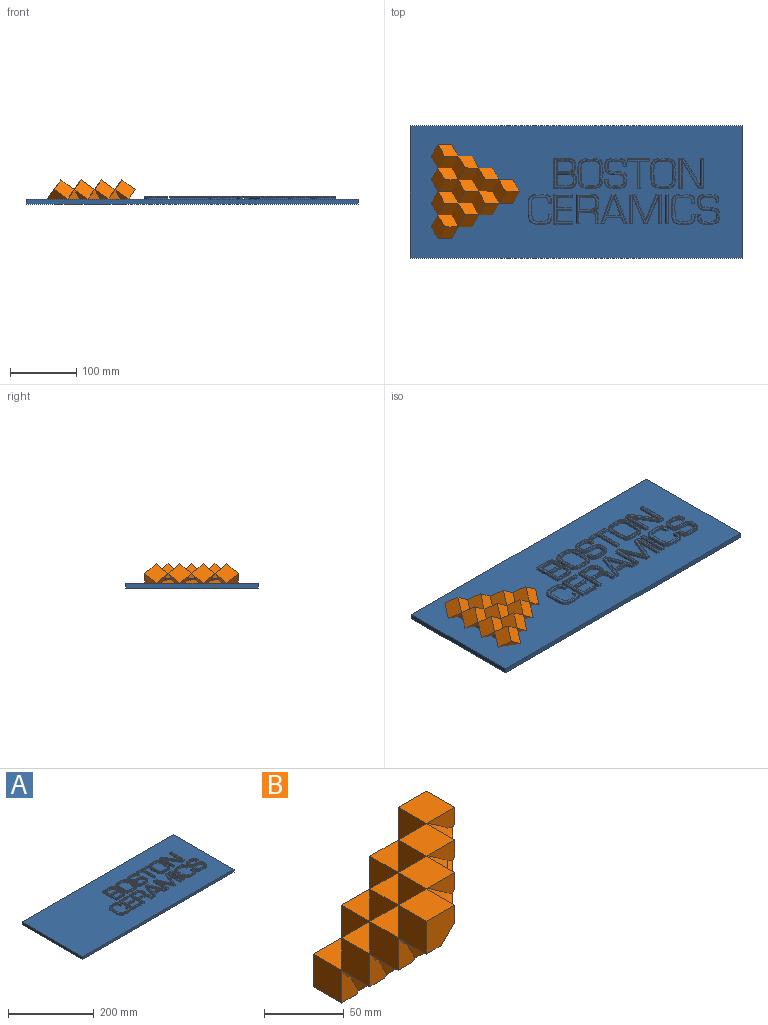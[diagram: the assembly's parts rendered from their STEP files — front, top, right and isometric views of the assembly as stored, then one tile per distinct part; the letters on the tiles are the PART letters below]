
ASSEMBLY  parts=2 mates=1
PART A: 238 faces, bbox 500x200x11.5 mm
  f0: cylinder r=1mm len=4.67mm, axis (-1,0,0), area 6.5mm2, adj f100,f101,f104,f198
  f1: cylinder r=1mm len=4.89mm, axis (1,0,0), area 6.9mm2, adj f100,f101,f102,f198
  f2: cylinder r=1mm len=4.67mm, axis (-1,0,0), area 6.5mm2, adj f119,f120,f123,f142
  f3: cylinder r=1mm len=4.89mm, axis (1,0,0), area 6.9mm2, adj f119,f120,f121,f142
  f4: plane 42.42x3.11mm, normal (0,0,1), area 132mm2, adj f147,f148,f150,f151
  f5: plane 42.42x39.02mm, normal (0,0,1), area 260mm2, adj f149,f151,f152,f155,f156,f158,f159
  f6: extruded ~16.02x7.64mm, area 77.2mm2, adj f7,f18,f20,f225
  f7: plane 16.61x3mm, normal (0,1,0), area 49.8mm2, adj f6,f8,f20,f226
  f8: plane 15.99x3mm, normal (1,0,0), area 48mm2, adj f7,f18,f20,f228
  f9: plane 20.32x3mm, normal (0,1,0), area 61mm2, adj f10,f16,f22,f232
  f10: plane 44.58x3mm, normal (-1,0,0), area 133.7mm2, adj f9,f11,f22,f230
  f11: plane 21.87x3mm, normal (0,-1,0), area 65.6mm2, adj f10,f12,f22,f229
  f12: extruded ~23.45x12.2mm, area 103.5mm2, adj f11,f16,f22,f231
  f13: plane 15.58x3mm, normal (0,-1,0), area 46.7mm2, adj f14,f17,f21,f235
  f14: extruded ~15.22x7.31mm, area 69.4mm2, adj f13,f15,f21,f234
  f15: plane 17.44x3mm, normal (0,1,0), area 52.3mm2, adj f14,f17,f21,f236
  f16: extruded ~21.25x12.24mm, area 96.5mm2, adj f9,f12,f22,f233
  f17: plane 15.17x3mm, normal (1,0,0), area 45.5mm2, adj f13,f15,f21,f237
  f18: plane 17.44x3mm, normal (0,-1,0), area 52.3mm2, adj f6,f8,f20,f227
  f19: plane 42.71x32.08mm, normal (0,0,1), area 407.7mm2, adj f225,f226,f227,f228,f229,f230,f231,f232
  f20: plane 24.31x16.07mm, normal (0,0,1), area 374.4mm2, adj f6,f7,f8,f18
  f21: plane 22.9x15.26mm, normal (0,0,1), area 333.6mm2, adj f13,f14,f15,f17
  f22: plane 500x200mm, normal (0,0,1), area 88572.9mm2, adj f9,f10,f11,f12,f16,f23,f24,f25
  f23: plane 33.72x3mm, normal (0,1,0), area 101.2mm2, adj f22,f24,f30,f214
  f24: plane 4.99x3mm, normal (-1,0.01,0), area 15mm2, adj f22,f23,f25,f212
  f25: plane 14.67x3mm, normal (0,-1,0), area 44mm2, adj f22,f24,f26,f211
  f26: plane 39.76x3mm, normal (-1,0,0), area 119.3mm2, adj f22,f25,f27,f213
  f27: plane 5x3mm, normal (0,-1,0), area 15mm2, adj f22,f26,f28,f215
  f28: plane 39.69x3mm, normal (1,0,0), area 119.1mm2, adj f22,f27,f29,f217
  f29: plane 14.1x3mm, normal (0,-1,0), area 42.3mm2, adj f22,f28,f30,f218
  f30: plane 5.06x3mm, normal (1,0,0), area 15.2mm2, adj f22,f23,f29,f216
  f31: plane 42.75x31.77mm, normal (0,0,1), area 215.4mm2, adj f211,f212,f213,f214,f215,f216,f217,f218
  f32: plane 4.89x3mm, normal (-0.01,-1,0), area 14.7mm2, adj f22,f33,f41,f204
  f33: plane 39.65x3mm, normal (1,0,0), area 118.9mm2, adj f22,f32,f34,f202
  f34: plane 39.63x24.41mm, normal (-0.85,-0.52,0), area 139.6mm2, adj f22,f33,f35,f200
  f35: plane 8.43x3mm, normal (-0.01,-1,0), area 25.3mm2, adj f22,f34,f36,f199
  f36: plane 44.65x3mm, normal (1,0,0), area 133.9mm2, adj f22,f35,f37,f201
  f37: plane 5.36x3mm, normal (0.01,1,0), area 16.1mm2, adj f22,f36,f38,f203
  f38: plane 40.02x3mm, normal (-1,0,0), area 120.1mm2, adj f22,f37,f39,f205
  f39: plane 39.93x24.4mm, normal (0.85,0.52,0), area 140.4mm2, adj f22,f38,f40,f207
  f40: plane 8.16x3mm, normal (0.01,1,0), area 24.5mm2, adj f22,f39,f41,f208
  f41: plane 44.58x3mm, normal (-1,0,0), area 133.7mm2, adj f22,f32,f40,f206
  f42: plane 42.68x35.92mm, normal (0,0,1), area 425.7mm2, adj f199,f200,f201,f202,f203,f204,f205,f206
  f43: plane 5.28x3mm, normal (0,1,0), area 15.8mm2, adj f22,f44,f46,f143
  f44: plane 44.42x3mm, normal (-1,0,0), area 133.3mm2, adj f22,f43,f45,f144
  f45: plane 5.28x3mm, normal (0,-1,0), area 15.8mm2, adj f22,f44,f46,f146
  f46: plane 44.42x3mm, normal (1,0,0), area 133.3mm2, adj f22,f43,f45,f145
  f47: plane 42.42x3.28mm, normal (0,0,1), area 139.1mm2, adj f143,f144,f145,f146
  f48: plane 5.06x3mm, normal (0,-1,0), area 15.2mm2, adj f22,f49,f60,f154
  f49: plane 44.42x3mm, normal (1,0,0), area 133.3mm2, adj f22,f48,f50,f153
  f50: plane 8.71x3mm, normal (0,1,0), area 26.1mm2, adj f22,f49,f51,f156
  f51: plane 37.97x15.71mm, normal (-0.92,0.38,0), area 123.3mm2, adj f22,f50,f52,f152
  f52: plane 37.97x15.54mm, normal (0.93,0.38,0), area 123.1mm2, adj f22,f51,f53,f149
  f53: plane 8.55x3mm, normal (0,1,0), area 25.6mm2, adj f22,f52,f54,f151
  f54: plane 44.42x3mm, normal (-1,0,0), area 133.3mm2, adj f22,f53,f55,f148
  f55: plane 5.11x3mm, normal (0,-1,0), area 15.3mm2, adj f22,f54,f56,f147
  f56: plane 39.95x3mm, normal (1,0,0), area 119.9mm2, adj f22,f55,f57,f150
  f57: plane 39.95x16.67mm, normal (-0.92,-0.39,0), area 129.9mm2, adj f22,f56,f58,f155
  f58: plane 4.99x3mm, normal (0,-1,0), area 15mm2, adj f22,f57,f59,f158
  f59: plane 39.95x16.64mm, normal (0.92,-0.38,0), area 129.8mm2, adj f22,f58,f60,f159
  f60: plane 39.95x3mm, normal (-1,0,0), area 119.9mm2, adj f22,f48,f59,f157
  f61: plane 42.42x3.1mm, normal (0,0,1), area 130.7mm2, adj f153,f154,f156,f157
  f62: plane 26.37x9.54mm, normal (0.94,-0.34,0), area 84.1mm2, adj f63,f72,f74,f160
  f63: plane 26.39x9.72mm, normal (-0.94,-0.35,0), area 84.4mm2, adj f62,f72,f74,f162
  f64: plane 6.73x3mm, normal (0,1,0), area 20.2mm2, adj f22,f65,f71,f168
  f65: plane 44.42x16.23mm, normal (-0.94,0.34,0), area 141.9mm2, adj f22,f64,f66,f166
  f66: plane 5.52x3mm, normal (0,-1,0), area 16.5mm2, adj f22,f65,f67,f164
  f67: plane 9.01x3.29mm, normal (0.94,-0.34,0), area 28.8mm2, adj f22,f66,f68,f163
  f68: plane 22.27x3mm, normal (0,-1,0), area 66.8mm2, adj f22,f67,f69,f165
  f69: plane 8.99x3.35mm, normal (-0.94,-0.35,0), area 28.8mm2, adj f22,f68,f70,f167
  f70: plane 5.34x3mm, normal (0,-1,0), area 16mm2, adj f22,f69,f71,f169
  f71: plane 44.42x16.81mm, normal (0.94,0.35,0), area 142.5mm2, adj f22,f64,f70,f170
  f72: plane 19.26x3mm, normal (0,1,0), area 57.8mm2, adj f62,f63,f74,f161
  f73: plane 42.42x36.89mm, normal (0,0,1), area 317.8mm2, adj f160,f161,f162,f163,f164,f165,f166,f167
  f74: plane 26.39x19.26mm, normal (0,0,1), area 254mm2, adj f62,f63,f72
  f75: extruded ~11.86x6.85mm, area 46.5mm2, adj f22,f76,f89,f178
  f76: extruded ~24.51x10.9mm, area 105.1mm2, adj f22,f75,f77,f176
  f77: plane 23.03x3mm, normal (0,1,0), area 69.1mm2, adj f22,f76,f78,f174
  f78: plane 44.44x3mm, normal (-1,0,0), area 133.3mm2, adj f22,f77,f79,f172
  f79: plane 4.81x3mm, normal (0,-1,0), area 14.4mm2, adj f22,f78,f80,f171
  f80: plane 17.8x3mm, normal (1,0,0), area 53.4mm2, adj f22,f79,f81,f173
  f81: plane 17.01x3mm, normal (0,-1,0), area 51mm2, adj f22,f80,f82,f175
  f82: extruded ~7.19x6.49mm, area 33mm2, adj f22,f81,f83,f177
  f83: plane 10.65x3mm, normal (-1,0,0), area 32mm2, adj f22,f82,f84,f179
  f84: plane 4.98x3mm, normal (0,-1,0), area 15mm2, adj f22,f83,f89,f181
  f85: plane 17.9x3mm, normal (0,-1,0), area 53.7mm2, adj f86,f88,f137,f183
  f86: extruded ~17.86x7.26mm, area 77.4mm2, adj f85,f87,f137,f182
  f87: plane 16.93x3mm, normal (0,1,0), area 50.8mm2, adj f86,f88,f137,f184
  f88: plane 17.74x3mm, normal (1,0,0), area 53.2mm2, adj f85,f87,f137,f185
  f89: plane 8.06x3mm, normal (1,0,0), area 24.2mm2, adj f22,f75,f84,f180
  f90: plane 42.44x31.93mm, normal (0,0,1), area 353.3mm2, adj f171,f172,f173,f174,f175,f176,f177,f178
  f91: plane 36.67x28.33mm, normal (0,0,1), area 965.5mm2, adj f113
  f92: extruded ~36.57x28.14mm, area 346.1mm2, adj f110,f209
  f93: extruded ~45.26x37.8mm, area 443.4mm2, adj f22,f210
  f94: plane 43.28x35.81mm, normal (0,0,1), area 330mm2, adj f209,f210
  f95: plane 500x200mm, normal (0,0,-1), area 100000mm2, adj f96,f97,f98,f99
  f96: plane 500x7.5mm, normal (0,-1,0), area 3750mm2, adj f22,f95,f97,f99
  f97: plane 200x7.5mm, normal (-1,0,0), area 1500mm2, adj f22,f95,f96,f98
  f98: plane 500x7.5mm, normal (0,1,0), area 3750mm2, adj f22,f95,f97,f99
  f99: plane 200x7.5mm, normal (1,0,0), area 1500mm2, adj f22,f95,f96,f98
  f100: plane 43.27x33.69mm, normal (0,0,1), area 409mm2, adj f0,f1,f101,f198
  f101: extruded ~36.26x25.62mm, area 382.1mm2, adj f0,f1,f22,f100,f102,f104
  f102: plane 4.89x3mm, normal (0,1,0), area 14.7mm2, adj f1,f22,f101,f103
  f103: extruded ~45.23x35.68mm, area 374.4mm2, adj f22,f102,f104,f198
  f104: plane 4.6x3mm, normal (0,-1,0), area 13.8mm2, adj f0,f22,f101,f103
  f105: plane 43.39x31.43mm, normal (0,0,1), area 343.4mm2, adj f138,f139,f140,f141
  f106: extruded ~40.76x33.41mm, area 380.7mm2, adj f22,f107,f109,f139
  f107: plane 5.01x3mm, normal (0,1,0), area 15mm2, adj f22,f106,f108,f141
  f108: extruded ~41.05x32.28mm, area 367.9mm2, adj f22,f107,f109,f140
  f109: plane 4.68x3mm, normal (0,-1,0), area 14mm2, adj f22,f106,f108,f138
  f110: plane 36.67x28.33mm, normal (0,0,1), area 965.5mm2, adj f92
  f111: plane 43.28x35.81mm, normal (0,0,1), area 330mm2, adj f223,f224
  f112: extruded ~45.26x37.8mm, area 443.4mm2, adj f22,f224
  f113: extruded ~36.57x28.14mm, area 346.1mm2, adj f91,f223
  f114: plane 43.39x31.43mm, normal (0,0,1), area 343.4mm2, adj f219,f220,f221,f222
  f115: extruded ~40.76x33.41mm, area 380.7mm2, adj f22,f116,f118,f220
  f116: plane 5.01x3mm, normal (0,1,0), area 15mm2, adj f22,f115,f117,f222
  f117: extruded ~41.05x32.28mm, area 367.9mm2, adj f22,f116,f118,f221
  f118: plane 4.68x3mm, normal (0,-1,0), area 14mm2, adj f22,f115,f117,f219
  f119: plane 43.27x33.69mm, normal (0,0,1), area 409mm2, adj f2,f3,f120,f142
  f120: extruded ~36.26x25.62mm, area 382.1mm2, adj f2,f3,f22,f119,f121,f123
  f121: plane 4.89x3mm, normal (0,1,0), area 14.7mm2, adj f3,f22,f120,f122
  f122: extruded ~45.23x35.68mm, area 374.4mm2, adj f22,f121,f123,f142
  f123: plane 4.6x3mm, normal (0,-1,0), area 13.8mm2, adj f2,f22,f120,f122
  f124: plane 42.54x26.48mm, normal (0,0,1), area 293.4mm2, adj f186,f187,f188,f189,f190,f191,f192,f193
  f125: plane 23.44x3mm, normal (0,-1,0), area 70.3mm2, adj f22,f126,f136,f195
  f126: plane 14.97x3mm, normal (1,0,0), area 44.9mm2, adj f22,f125,f127,f197
  f127: plane 22.3x3mm, normal (0,1,0), area 66.9mm2, adj f22,f126,f128,f196
  f128: plane 4.48x3mm, normal (1,0,0), area 13.4mm2, adj f22,f127,f129,f194
  f129: plane 22.3x3mm, normal (0,-1,0), area 66.9mm2, adj f22,f128,f130,f192
  f130: plane 16.44x3mm, normal (1,0,0), area 49.3mm2, adj f22,f129,f131,f190
  f131: plane 23.28x3mm, normal (0,1,0), area 69.8mm2, adj f22,f130,f132,f188
  f132: plane 4.31x3mm, normal (1,0,0), area 12.9mm2, adj f22,f131,f133,f186
  f133: plane 28.32x3mm, normal (0,-1,0), area 85mm2, adj f22,f132,f134,f187
  f134: plane 44.54x3mm, normal (-1,0,0), area 133.6mm2, adj f22,f133,f135,f189
  f135: plane 28.48x3mm, normal (0,1,0), area 85.4mm2, adj f22,f134,f136,f191
  f136: plane 4.34x3mm, normal (1,0,0), area 13mm2, adj f22,f125,f135,f193
  f137: plane 24.24x17.91mm, normal (0,0,1), area 410.3mm2, adj f85,f86,f87,f88
  f138: cylinder r=1mm len=4.68mm, axis (-1,0,0), area 5.9mm2, adj f105,f109,f139,f140
  f139: bspline ~41.76x33.43mm, area 197.6mm2, adj f105,f106,f138,f141
  f140: bspline ~42.11x32.36mm, area 197.9mm2, adj f105,f108,f138,f141
  f141: cylinder r=1mm len=5.01mm, axis (1,0,0), area 6.4mm2, adj f105,f107,f139,f140
  f142: bspline ~45.27x35.69mm, area 193.2mm2, adj f2,f3,f119,f122
  f143: cylinder r=1mm len=5.28mm, axis (1,0,0), area 6.7mm2, adj f43,f47,f144,f145
  f144: cylinder r=1mm len=44.42mm, axis (0,1,0), area 68.2mm2, adj f44,f47,f143,f146
  f145: cylinder r=1mm len=44.42mm, axis (0,-1,0), area 68.2mm2, adj f46,f47,f143,f146
  f146: cylinder r=1mm len=5.28mm, axis (-1,0,0), area 6.7mm2, adj f45,f47,f144,f145
  f147: cylinder r=1mm len=5.11mm, axis (-1,0,0), area 6.5mm2, adj f4,f55,f148,f150
  f148: cylinder r=1mm len=44.42mm, axis (0,1,0), area 68.2mm2, adj f4,f54,f147,f151
  f149: cylinder r=1mm len=40.6mm, axis (0.38,-0.93,0), area 65.8mm2, adj f5,f52,f151,f152
  f150: cylinder r=1mm len=43.68mm, axis (0,-1,0), area 64.8mm2, adj f4,f56,f147,f151,f155
  f151: cylinder r=1mm len=8.55mm, axis (1,0,0), area 12.2mm2, adj f4,f5,f53,f148,f149,f150,f155
  f152: cylinder r=1mm len=40.6mm, axis (0.38,0.92,0), area 65.9mm2, adj f5,f51,f149,f156
  f153: cylinder r=1mm len=44.42mm, axis (0,-1,0), area 68.2mm2, adj f49,f61,f154,f156
  f154: cylinder r=1mm len=5.06mm, axis (-1,0,0), area 6.4mm2, adj f48,f61,f153,f157
  f155: cylinder r=1mm len=43.78mm, axis (-0.39,0.92,0), area 70.1mm2, adj f5,f57,f150,f151,f158
  f156: cylinder r=1mm len=8.71mm, axis (1,0,0), area 12.5mm2, adj f5,f50,f61,f152,f153,f157,f159
  f157: cylinder r=1mm len=43.68mm, axis (0,1,0), area 64.8mm2, adj f60,f61,f154,f156,f159
  f158: cylinder r=1mm len=4.99mm, axis (-1,0,0), area 6.8mm2, adj f5,f58,f155,f159
  f159: cylinder r=1mm len=43.78mm, axis (-0.38,-0.92,0), area 70.1mm2, adj f5,f59,f156,f157,f158
  f160: cylinder r=1mm len=30.63mm, axis (-0.34,-0.94,0), area 47.3mm2, adj f62,f73,f161,f162
  f161: cylinder r=1mm len=22.12mm, axis (1,0,0), area 32.5mm2, adj f72,f73,f160,f162
  f162: cylinder r=1mm len=30.65mm, axis (-0.35,0.94,0), area 47.4mm2, adj f63,f73,f160,f161
  f163: cylinder r=1mm len=10.01mm, axis (-0.34,-0.94,0), area 15.1mm2, adj f67,f73,f164,f165
  f164: cylinder r=1mm len=5.52mm, axis (-1,0,0), area 7mm2, adj f66,f73,f163,f166
  f165: cylinder r=1mm len=23.67mm, axis (-1,0,0), area 36.1mm2, adj f68,f73,f163,f167
  f166: cylinder r=1mm len=44.76mm, axis (0.34,0.94,0), area 72.6mm2, adj f65,f73,f164,f168
  f167: cylinder r=1mm len=9.99mm, axis (-0.35,0.94,0), area 15.1mm2, adj f69,f73,f165,f169
  f168: cylinder r=1mm len=6.73mm, axis (1,0,0), area 9.5mm2, adj f64,f73,f166,f170
  f169: cylinder r=1mm len=5.34mm, axis (-1,0,0), area 6.7mm2, adj f70,f73,f167,f170
  f170: cylinder r=1mm len=44.77mm, axis (0.35,-0.94,0), area 72.9mm2, adj f71,f73,f168,f169
  f171: cylinder r=1mm len=4.81mm, axis (-1,0,0), area 6mm2, adj f79,f90,f172,f173
  f172: cylinder r=1mm len=44.44mm, axis (0,1,0), area 68.2mm2, adj f78,f90,f171,f174
  f173: cylinder r=1mm len=18.81mm, axis (0,-1,0), area 28mm2, adj f80,f90,f171,f175
  f174: cylinder r=1mm len=23.03mm, axis (1,0,0), area 35.4mm2, adj f77,f90,f172,f176
  f175: cylinder r=1mm len=18.01mm, axis (-1,0,0), area 27.5mm2, adj f81,f90,f173,f177
  f176: bspline ~25.88x13.96mm, area 57.5mm2, adj f76,f90,f174,f178
  f177: bspline ~8.67x7.78mm, area 18.2mm2, adj f82,f90,f175,f179
  f178: bspline ~24.13x15.38mm, area 27.7mm2, adj f75,f90,f176,f180
  f179: cylinder r=1mm len=10.65mm, axis (0,1,0), area 15.9mm2, adj f83,f90,f177,f181
  f180: cylinder r=1mm len=8.09mm, axis (0,-1,0), area 11.9mm2, adj f89,f90,f178,f181
  f181: cylinder r=1mm len=4.98mm, axis (-1,0,0), area 6.3mm2, adj f84,f90,f179,f180
  f182: bspline ~19.95x10.14mm, area 42.4mm2, adj f86,f90,f183,f184
  f183: cylinder r=1mm len=18.9mm, axis (-1,0,0), area 28.8mm2, adj f85,f90,f182,f185
  f184: cylinder r=1mm len=17.95mm, axis (1,0,0), area 27.4mm2, adj f87,f90,f182,f185
  f185: cylinder r=1mm len=19.74mm, axis (0,-1,0), area 29.4mm2, adj f88,f90,f183,f184
  f186: cylinder r=1mm len=4.31mm, axis (0,-1,0), area 5.2mm2, adj f124,f132,f187,f188
  f187: cylinder r=1mm len=28.32mm, axis (-1,0,0), area 42.9mm2, adj f124,f133,f186,f189
  f188: cylinder r=1mm len=24.28mm, axis (1,0,0), area 36.6mm2, adj f124,f131,f186,f190
  f189: cylinder r=1mm len=44.54mm, axis (0,1,0), area 68.4mm2, adj f124,f134,f187,f191
  f190: cylinder r=1mm len=18.44mm, axis (0,-1,0), area 27.4mm2, adj f124,f130,f188,f192
  f191: cylinder r=1mm len=28.48mm, axis (1,0,0), area 43.2mm2, adj f124,f135,f189,f193
  f192: cylinder r=1mm len=23.3mm, axis (-1,0,0), area 35mm2, adj f124,f129,f190,f194
  f193: cylinder r=1mm len=4.34mm, axis (0,-1,0), area 5.2mm2, adj f124,f136,f191,f195
  f194: cylinder r=1mm len=4.48mm, axis (0,-1,0), area 5.5mm2, adj f124,f128,f192,f196
  f195: cylinder r=1mm len=24.44mm, axis (-1,0,0), area 36.8mm2, adj f124,f125,f193,f197
  f196: cylinder r=1mm len=23.3mm, axis (1,0,0), area 35mm2, adj f124,f127,f194,f197
  f197: cylinder r=1mm len=16.97mm, axis (0,-1,0), area 25.1mm2, adj f124,f126,f195,f196
  f198: bspline ~45.27x35.69mm, area 193.2mm2, adj f0,f1,f100,f103
  f199: cylinder r=1mm len=8.44mm, axis (-1,0.01,0), area 12mm2, adj f35,f42,f200,f201
  f200: cylinder r=1mm len=43.13mm, axis (-0.52,0.85,0), area 75.4mm2, adj f34,f42,f199,f202
  f201: cylinder r=1mm len=44.65mm, axis (0,-1,0), area 68.6mm2, adj f36,f42,f199,f203
  f202: cylinder r=1mm len=43.15mm, axis (0,-1,0), area 64.2mm2, adj f33,f42,f200,f204
  f203: cylinder r=1mm len=5.37mm, axis (1,-0.01,0), area 6.8mm2, adj f37,f42,f201,f205
  f204: cylinder r=1mm len=4.9mm, axis (-1,0.01,0), area 6.1mm2, adj f32,f42,f202,f206
  f205: cylinder r=1mm len=43.58mm, axis (0,1,0), area 64.9mm2, adj f38,f42,f203,f207
  f206: cylinder r=1mm len=44.58mm, axis (0,1,0), area 68.5mm2, adj f41,f42,f204,f208
  f207: cylinder r=1mm len=43.49mm, axis (0.52,-0.85,0), area 75.9mm2, adj f39,f42,f205,f208
  f208: cylinder r=1mm len=8.17mm, axis (1,-0.01,0), area 11.6mm2, adj f40,f42,f206,f207
  f209: bspline ~38.58x30.17mm, area 186mm2, adj f92,f94
  f210: bspline ~45.28x37.81mm, area 223.6mm2, adj f93,f94
  f211: cylinder r=1mm len=15.67mm, axis (-1,0,0), area 23mm2, adj f25,f31,f212,f213
  f212: cylinder r=1mm len=5mm, axis (0.01,1,0), area 6.3mm2, adj f24,f31,f211,f214
  f213: cylinder r=1mm len=40.76mm, axis (0,1,0), area 62.5mm2, adj f26,f31,f211,f215
  f214: cylinder r=1mm len=33.72mm, axis (1,0,0), area 51.4mm2, adj f23,f31,f212,f216
  f215: cylinder r=1mm len=5mm, axis (-1,0,0), area 6.3mm2, adj f27,f31,f213,f217
  f216: cylinder r=1mm len=5.06mm, axis (0,-1,0), area 6.4mm2, adj f30,f31,f214,f218
  f217: cylinder r=1mm len=40.69mm, axis (0,-1,0), area 62.3mm2, adj f28,f31,f215,f218
  f218: cylinder r=1mm len=15.1mm, axis (-1,0,0), area 22.1mm2, adj f29,f31,f216,f217
  f219: cylinder r=1mm len=4.68mm, axis (-1,0,0), area 5.9mm2, adj f114,f118,f220,f221
  f220: bspline ~41.76x33.43mm, area 197.6mm2, adj f114,f115,f219,f222
  f221: bspline ~42.11x32.36mm, area 197.9mm2, adj f114,f117,f219,f222
  f222: cylinder r=1mm len=5.01mm, axis (1,0,0), area 6.4mm2, adj f114,f116,f220,f221
  f223: bspline ~38.58x30.17mm, area 186mm2, adj f111,f113
  f224: bspline ~45.28x37.81mm, area 223.6mm2, adj f111,f112
  f225: bspline ~18.04x9.28mm, area 42.2mm2, adj f6,f19,f226,f227
  f226: cylinder r=1mm len=17.63mm, axis (1,0,0), area 26.9mm2, adj f7,f19,f225,f228
  f227: cylinder r=1mm len=18.44mm, axis (-1,0,0), area 28.2mm2, adj f18,f19,f225,f228
  f228: cylinder r=1mm len=17.99mm, axis (0,-1,0), area 26.7mm2, adj f8,f19,f226,f227
  f229: cylinder r=1mm len=21.92mm, axis (-1,0,0), area 33.6mm2, adj f11,f19,f230,f231
  f230: cylinder r=1mm len=44.58mm, axis (0,1,0), area 68.5mm2, adj f10,f19,f229,f232
  f231: bspline ~26.17x15.33mm, area 54.5mm2, adj f12,f19,f229,f233
  f232: cylinder r=1mm len=20.32mm, axis (1,0,0), area 31.1mm2, adj f9,f19,f230,f233
  f233: bspline ~23.51x14.63mm, area 50.9mm2, adj f16,f19,f231,f232
  f234: bspline ~17.35x8.85mm, area 38.1mm2, adj f14,f19,f235,f236
  f235: cylinder r=1mm len=16.58mm, axis (-1,0,0), area 25.2mm2, adj f13,f19,f234,f237
  f236: cylinder r=1mm len=18.53mm, axis (1,0,0), area 28.3mm2, adj f15,f19,f234,f237
  f237: cylinder r=1mm len=17.17mm, axis (0,-1,0), area 25.4mm2, adj f17,f19,f235,f236
PART B: 79 faces, bbox 100x100x100 mm
  f0: plane 23.19x23.19mm, normal (0.41,0.82,-0.41), area 279.7mm2, adj f14,f25,f77,f78
  f1: plane 23.19x23.19mm, normal (0.41,0.82,-0.41), area 279.7mm2, adj f23,f27,f76,f78
  f2: plane 23.19x23.19mm, normal (-0.82,-0.41,-0.41), area 279.1mm2, adj f7,f20,f74,f78
  f3: plane 23.19x23.19mm, normal (-0.82,-0.41,-0.41), area 279.1mm2, adj f6,f22,f73,f78
  f4: plane 23.19x23.19mm, normal (0.41,-0.41,0.82), area 105.9mm2, adj f8,f9,f19,f78
  f5: plane 23.19x23.19mm, normal (0.41,-0.41,0.82), area 105.9mm2, adj f11,f12,f18,f78
  f6: plane 24.66x14.91mm, normal (0,-1,0), area 217.6mm2, adj f3,f20,f31,f33,f55,f73,f78
  f7: plane 24.66x14.91mm, normal (0,-1,0), area 217.6mm2, adj f2,f28,f30,f33,f54,f74,f78
  f8: plane 24.09x14.91mm, normal (1,0,0), area 199.2mm2, adj f4,f19,f32,f34,f78
  f9: plane 24.09x14.91mm, normal (0,-1,0), area 199.2mm2, adj f4,f11,f19,f34,f78
  f10: plane 24.66x14.91mm, normal (0,-1,0), area 217.6mm2, adj f22,f33,f53,f56,f64,f72,f78
  f11: plane 24.09x14.91mm, normal (1,0,0), area 199.2mm2, adj f5,f9,f18,f34,f78
  f12: plane 24.09x14.91mm, normal (0,-1,0), area 199.2mm2, adj f5,f13,f18,f34,f78
  f13: plane 24.09x14.91mm, normal (1,0,0), area 199.2mm2, adj f12,f17,f34,f65,f78
  f14: plane 24.64x14.91mm, normal (1,0,0), area 215.8mm2, adj f0,f23,f29,f57,f62,f77,f78
  f15: plane 24.09x14.91mm, normal (0,-1,0), area 199.2mm2, adj f16,f17,f34,f65,f78
  f16: plane 25x25mm, normal (1,0,0), area 554.3mm2, adj f15,f25,f29,f34,f78
  f17: plane 19.1x19.1mm, normal (0.5,-0.5,0.71), area 257.5mm2, adj f13,f15,f34,f65
  f18: plane 19.1x19.1mm, normal (0.5,-0.5,0.71), area 257.5mm2, adj f5,f11,f12,f34
  f19: plane 19.1x19.1mm, normal (0.5,-0.5,0.71), area 257.5mm2, adj f4,f8,f9,f34
  f20: plane 24.65x14.91mm, normal (0,0,-1), area 215.3mm2, adj f2,f6,f30,f33,f54,f74,f78
  f21: plane 24.65x14.91mm, normal (0,0,-1), area 216.8mm2, adj f27,f29,f58,f60,f63,f75,f78
  f22: plane 24.65x14.91mm, normal (0,0,-1), area 215.3mm2, adj f3,f10,f31,f33,f55,f73,f78
  f23: plane 24.65x14.91mm, normal (0,0,-1), area 216.8mm2, adj f1,f14,f29,f59,f61,f76,f78
  f24: plane 24.65x14.91mm, normal (0,0,-1), area 215.3mm2, adj f32,f33,f53,f56,f64,f72,f78
  f25: plane 24.65x14.91mm, normal (0,0,-1), area 216.8mm2, adj f0,f16,f29,f57,f62,f77,f78
  f26: plane 24.64x14.91mm, normal (1,0,0), area 215.8mm2, adj f28,f29,f58,f60,f63,f75,f78
  f27: plane 24.64x14.91mm, normal (1,0,0), area 215.8mm2, adj f1,f21,f29,f59,f61,f76,f78
  f28: plane 25x25mm, normal (0,0,-1), area 554.3mm2, adj f7,f26,f29,f33,f78
  f29: plane 100x100mm, normal (0,1,0), area 2500.2mm2, adj f14,f16,f21,f23,f25,f26,f27,f28
  f30: plane 7.58x7.26mm, normal (0,-0.69,-0.72), area 25.9mm2, adj f7,f20,f54,f74
  f31: plane 7.58x7.26mm, normal (0,-0.69,-0.72), area 25.9mm2, adj f6,f22,f55,f73
  f32: plane 25x25mm, normal (0,-1,0), area 554.3mm2, adj f8,f24,f33,f34,f78
  f33: plane 100x100mm, normal (-1,0,0), area 2500.2mm2, adj f6,f7,f10,f20,f22,f24,f28,f29
  f34: plane 100x100mm, normal (0,0,1), area 2501.2mm2, adj f8,f9,f11,f12,f13,f15,f16,f17
  f35: plane 25x25mm, normal (-1,0,0), area 625mm2, adj f34,f36,f46,f50,f68
  f36: plane 25x25mm, normal (0,1,0), area 625mm2, adj f34,f35,f46,f48,f68
  f37: plane 25x25mm, normal (0,1,0), area 625mm2, adj f41,f42,f44,f46,f70
  f38: plane 25x25mm, normal (0,1,0), area 625mm2, adj f33,f39,f40,f45,f71
  f39: plane 25x25mm, normal (-1,0,0), area 625mm2, adj f29,f38,f40,f42,f71
  f40: plane 25x25mm, normal (0,0,1), area 625mm2, adj f29,f33,f38,f39,f71
  f41: plane 25x25mm, normal (-1,0,0), area 625mm2, adj f29,f37,f42,f52,f70
  f42: plane 25x25mm, normal (0,0,1), area 625mm2, adj f29,f37,f39,f41,f70
  f43: plane 25x25mm, normal (0,1,0), area 625mm2, adj f33,f44,f45,f49,f69
  f44: plane 25x25mm, normal (-1,0,0), area 625mm2, adj f37,f43,f45,f46,f69
  f45: plane 25x25mm, normal (0,0,1), area 625mm2, adj f33,f38,f43,f44,f69
  f46: plane 25x25mm, normal (0,0,1), area 625mm2, adj f35,f36,f37,f44,f68
  f47: plane 25x25mm, normal (0,1,0), area 625mm2, adj f33,f34,f48,f49,f67
  f48: plane 25x25mm, normal (-1,0,0), area 625mm2, adj f34,f36,f47,f49,f67
  f49: plane 25x25mm, normal (0,0,1), area 625mm2, adj f33,f43,f47,f48,f67
  f50: plane 25x25mm, normal (0,1,0), area 625mm2, adj f34,f35,f51,f52,f66
  f51: plane 25x25mm, normal (-1,0,0), area 625mm2, adj f29,f34,f50,f52,f66
  f52: plane 25x25mm, normal (0,0,1), area 625mm2, adj f29,f41,f50,f51,f66
  f53: plane 7.58x7.26mm, normal (0,-0.69,-0.72), area 25.9mm2, adj f10,f24,f56,f72
  f54: plane 7.58x7.26mm, normal (-0.71,-0.49,-0.51), area 38.9mm2, adj f7,f20,f30,f33
  f55: plane 7.58x7.26mm, normal (-0.71,-0.49,-0.51), area 38.9mm2, adj f6,f22,f31,f33
  f56: plane 7.58x7.26mm, normal (-0.71,-0.49,-0.51), area 38.9mm2, adj f10,f24,f33,f53
  f57: plane 7.49x7.36mm, normal (0.71,0,-0.7), area 25.8mm2, adj f14,f25,f62,f77
  f58: plane 7.49x7.36mm, normal (0.71,0,-0.7), area 25.8mm2, adj f21,f26,f60,f75
  f59: plane 7.49x7.36mm, normal (0.71,0,-0.7), area 25.8mm2, adj f23,f27,f61,f76
  f60: plane 7.49x7.36mm, normal (0.5,0.71,-0.5), area 38.9mm2, adj f21,f26,f29,f58
  f61: plane 7.49x7.36mm, normal (0.5,0.71,-0.5), area 38.9mm2, adj f23,f27,f29,f59
  f62: plane 7.49x7.36mm, normal (0.5,0.71,-0.5), area 38.9mm2, adj f14,f25,f29,f57
  f63: plane 23.19x23.19mm, normal (0.41,0.82,-0.41), area 279.7mm2, adj f21,f26,f75,f78
  f64: plane 23.19x23.19mm, normal (-0.82,-0.41,-0.41), area 279.1mm2, adj f10,f24,f72,f78
  f65: plane 23.19x23.19mm, normal (0.41,-0.41,0.82), area 105.9mm2, adj f13,f15,f17,f78
  f66: plane 0.11x0.11mm, normal (-0.58,0.58,0.58), area 0mm2, adj f50,f51,f52
  f67: plane 0.11x0.11mm, normal (-0.58,0.58,0.58), area 0mm2, adj f47,f48,f49
  f68: plane 0.11x0.11mm, normal (-0.58,0.58,0.58), area 0mm2, adj f35,f36,f46
  f69: plane 0.11x0.11mm, normal (-0.58,0.58,0.58), area 0mm2, adj f43,f44,f45
  f70: plane 0.11x0.11mm, normal (-0.58,0.58,0.58), area 0mm2, adj f37,f41,f42
  f71: plane 0.11x0.11mm, normal (-0.58,0.58,0.58), area 0mm2, adj f38,f39,f40
  f72: plane 9.98x8.23mm, normal (-0.95,-0.19,-0.24), area 14.2mm2, adj f10,f24,f53,f64
  f73: plane 9.98x8.23mm, normal (-0.95,-0.19,-0.24), area 14.2mm2, adj f3,f6,f22,f31
  f74: plane 9.98x8.23mm, normal (-0.95,-0.19,-0.24), area 14.2mm2, adj f2,f7,f20,f30
  f75: plane 9.37x8.66mm, normal (0.22,0.95,-0.2), area 13.7mm2, adj f21,f26,f58,f63
  f76: plane 9.37x8.66mm, normal (0.22,0.95,-0.2), area 13.7mm2, adj f1,f23,f27,f59
  f77: plane 9.37x8.66mm, normal (0.22,0.95,-0.2), area 13.7mm2, adj f0,f14,f25,f57
  f78: plane 86.9x86.9mm, normal (0.58,-0.58,-0.58), area 7405.8mm2, adj f0,f1,f2,f3,f4,f5,f6,f7
PLACE A rot(axis=(-0.65,0.73,-0.18),0deg) t=(-151.82,32.61,46.59)mm
PLACE B rot(axis=(0.77,0.59,-0.24),56.6deg) t=(-460.26,40.84,1.78)mm
MATE planar A.f95 <-> B.f78  axis (0,0,-1) through (-226.82,32.61,39.09)mm
